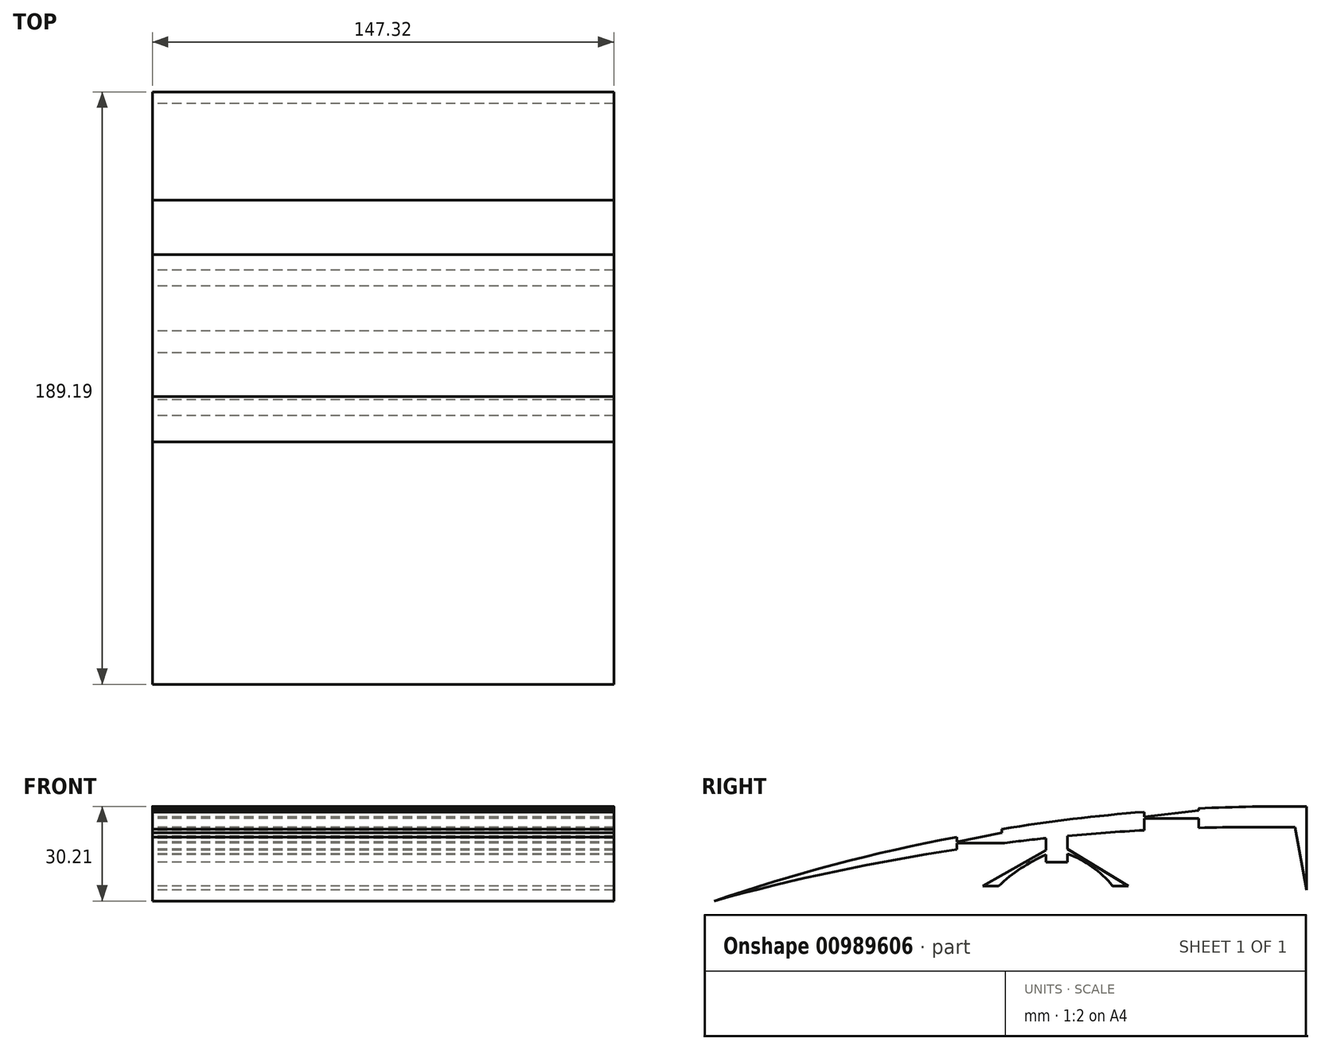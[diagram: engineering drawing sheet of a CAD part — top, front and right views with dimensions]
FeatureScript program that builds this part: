
annotation { "Feature Type Name" : "Feature", "Feature Type Description" : "" }
export const myFeature = defineFeature(function(context is Context, id is Id, definition is map)
    precondition{}
    {
        {
            var Q0;
            Q0=qCreatedBy(makeId("Right.planeOp"),FACE);
            var sketch = newSketch(context, id + "F0", { "sketchPlane" : qUnion([Q0])});
            skArc(sketch, "E0", {"start": v(102.7, 0.73) * mm, "mid": v(85.43, 0.7) * mm, "end": v(68.17, 0.13) * mm});
            skLineSegment(sketch, "E1", {"start": v(102.7, 0.73) * mm, "end": v(102.7, -25.94) * mm});
            skPoint(sketch, "E1.startSnap0", {"position": v(102.7, 0.73) * mm});
            skPoint(sketch, "E2.orphan", {"position": v(102.7, 24.97) * mm});
            skArc(sketch, "E3", {"start": v(99.02, -5.91) * mm, "mid": v(83.6, -5.82) * mm, "end": v(68.17, -6.1) * mm});
            skLineSegment(sketch, "E4", {"start": v(99.02, -5.91) * mm, "end": v(102.7, -25.94) * mm});
            skLineSegment(sketch, "E5", {"start": v(-9.03, -12.99) * mm, "end": v(-9.03, -11) * mm});
            skPoint(sketch, "E5.endSnap0", {"position": v(5.42, -11) * mm});
            skLineSegment(sketch, "E6", {"start": v(-9.03, -11) * mm, "end": v(5.42, -11) * mm});
            skLineSegment(sketch, "E7", {"start": v(50.79, -6.84) * mm, "end": v(50.79, -3.02) * mm});
            skLineSegment(sketch, "E8", {"start": v(50.79, -3.02) * mm, "end": v(68.17, -3.02) * mm});
            skLineSegment(sketch, "E9", {"start": v(68.17, -3.02) * mm, "end": v(68.17, -6.1) * mm});
            skPoint(sketch, "E10.start.orphan", {"position": v(68.17, -11) * mm});
            skArc(sketch, "E11.trimOffspring", {"start": v(50.79, -6.84) * mm, "mid": v(38.56, -7.65) * mm, "end": v(26.34, -8.68) * mm});
            skArc(sketch, "E12.trimOffspring", {"start": v(-9.03, -12.99) * mm, "mid": v(-48.01, -20.03) * mm, "end": v(-86.5, -29.43) * mm});
            skLineSegment(sketch, "E13", {"start": v(50.79, -2.56) * mm, "end": v(50.79, -0.98) * mm});
            skLineSegment(sketch, "E14", {"start": v(68.17, -0.55) * mm, "end": v(68.17, 0.13) * mm});
            skLineSegment(sketch, "E15", {"start": v(50.79, -2.56) * mm, "end": v(68.17, -0.55) * mm});
            skArc(sketch, "E16.trimOffspring", {"start": v(50.79, -0.98) * mm, "mid": v(28.05, -3.25) * mm, "end": v(5.42, -6.44) * mm});
            skLineSegment(sketch, "E17", {"start": v(-9.03, -10.55) * mm, "end": v(-9.03, -8.98) * mm});
            skLineSegment(sketch, "E18", {"start": v(5.42, -7.66) * mm, "end": v(5.42, -6.44) * mm});
            skLineSegment(sketch, "E19", {"start": v(-9.03, -10.55) * mm, "end": v(5.42, -7.66) * mm});
            skArc(sketch, "E20.trimOffspring", {"start": v(-9.03, -8.98) * mm, "mid": v(-48.13, -17.82) * mm, "end": v(-86.5, -29.43) * mm});
            skLineSegment(sketch, "E21", {"start": v(102.7, -25.94) * mm, "end": v(-21.3, -25.94) * mm});
            skLineSegment(sketch, "E22", {"start": v(19.41, -9.37) * mm, "end": v(19.41, -13.2) * mm});
            skLineSegment(sketch, "E23", {"start": v(26.34, -8.68) * mm, "end": v(26.34, -12.86) * mm});
            skLineSegment(sketch, "E24", {"start": v(19.41, -17.03) * mm, "end": v(26.34, -17.03) * mm});
            skLineSegment(sketch, "E25", {"start": v(19.41, -13.2) * mm, "end": v(-0.72, -24.61) * mm});
            skLineSegment(sketch, "E26", {"start": v(-0.72, -24.61) * mm, "end": v(4.36, -24.61) * mm});
            skArc(sketch, "E27", {"start": v(19.41, -14.63) * mm, "mid": v(11.47, -19) * mm, "end": v(4.36, -24.61) * mm});
            skLineSegment(sketch, "E28", {"start": v(40.73, -24.61) * mm, "end": v(45.81, -24.61) * mm});
            skLineSegment(sketch, "E29", {"start": v(26.34, -12.86) * mm, "end": v(45.81, -24.61) * mm});
            skArc(sketch, "E30", {"start": v(40.73, -24.61) * mm, "mid": v(34.23, -18.51) * mm, "end": v(26.34, -14.37) * mm});
            skLineSegment(sketch, "E31.trimOffspring", {"start": v(26.34, -14.37) * mm, "end": v(26.34, -17.03) * mm});
            skLineSegment(sketch, "E32.trimOffspring", {"start": v(19.41, -14.63) * mm, "end": v(19.41, -17.03) * mm});
            skArc(sketch, "E33.trimOffspring", {"start": v(19.41, -9.37) * mm, "mid": v(12.4, -10.14) * mm, "end": v(5.42, -11) * mm});
            skSolve(sketch);
        }
        {
            var Q0;
            Q0 = qSketchRegion(id + "F0", true);
            extrude(context, id + "F1", {"entities" : qUnion([Q0]), "depth" : 147.32 * mm, "offsetDistance" : 25.4 * mm});
        }
    });
